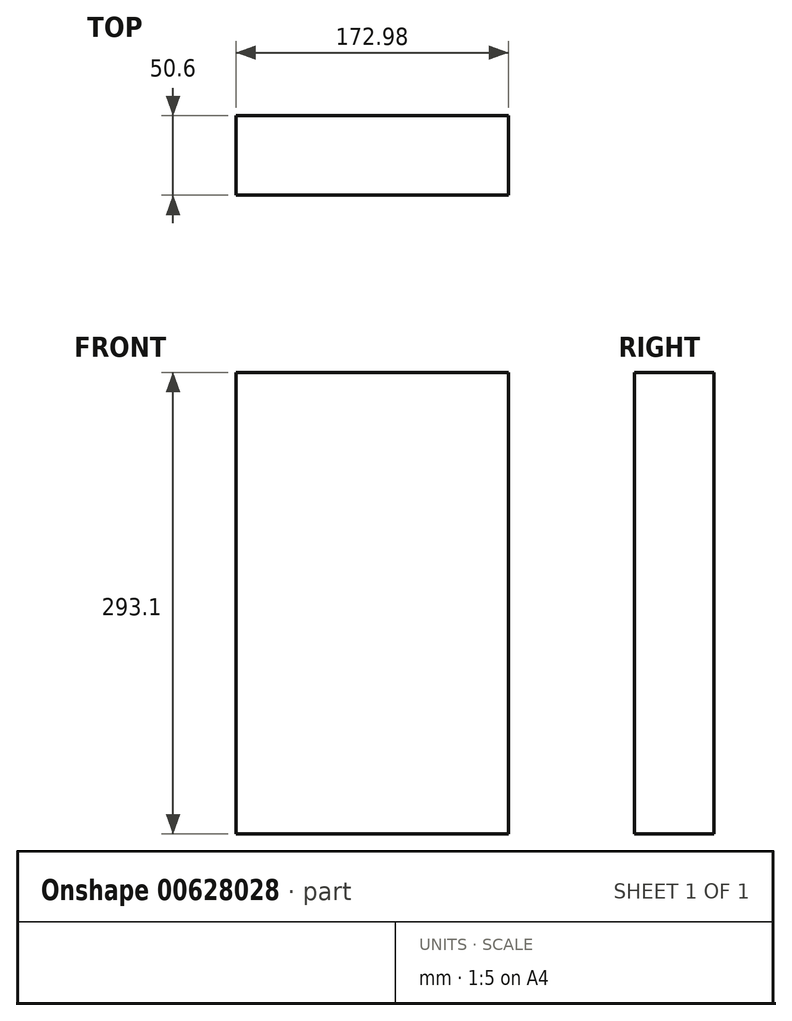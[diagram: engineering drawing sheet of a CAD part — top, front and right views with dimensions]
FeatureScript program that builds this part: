
annotation { "Feature Type Name" : "Feature", "Feature Type Description" : "" }
export const myFeature = defineFeature(function(context is Context, id is Id, definition is map)
    precondition{}
    {
        {
            var Q0;
            Q0=qCreatedBy(makeId("Top.planeOp"),FACE);
            var sketch = newSketch(context, id + "F0", { "sketchPlane" : qUnion([Q0])});
            skLineSegment(sketch, "E0.bottom", {"start": v(-86.5, 25.3) * mm, "end": v(86.5, 25.3) * mm});
            skLineSegment(sketch, "E0.top", {"start": v(-86.5, -25.3) * mm, "end": v(86.5, -25.3) * mm});
            skLineSegment(sketch, "E0.left", {"start": v(-86.5, 25.3) * mm, "end": v(-86.5, -25.3) * mm});
            skLineSegment(sketch, "E0.right", {"start": v(86.5, 25.3) * mm, "end": v(86.5, -25.3) * mm});
            skPoint(sketch, "E0.middle", {"position": v(0, 0) * mm});
            skSolve(sketch);
        }
        {
            var Q0;
            Q0 = qSketchRegion(id + "F0", true);
            extrude(context, id + "F1", {"entities" : qUnion([Q0]), "depth" : 293.1 * mm, "offsetDistance" : 25.4 * mm});
        }
    });
